# Revit family: H9726-V3
name_source: partatom
category: Plumbing Fixtures
revit_build: Autodesk Revit 2015 (Build: 20140606_1530(x64)
units: mm (PartAtom-declared; Revit-internal decimal feet)

## types (1)
- H9726-V3
    Category = Basin mixer
    DLB090016 = Brass, Chrome plated
    Default Elevation = 1219 mm
    Description = French manufacturer Delabie is a leader in the European sanitary ware market for non-domestic places. Water controls, solutions for disabled people, sanitary ware, for schools, leisure centres, offices, hospitals, airports…
    Diameter = 15 mm  [stored 0.0492126 ft]
    Features = Deck-mounted SECURITHERM dual control thermostatic basin mixer, with ergonomic pop-up waste 1 1/4" in brass.  Anti-scalding failsafe: hot water shuts off immediately if cold water supply fails. Swivelling spout L. 150mm H. 210mm with smooth interior and with BIOSAFE hygienic outlet, suitable for fitting a BIOFIL filter (reduces bacterial development).  Scale-resistant thermostatic cartridge for temperature control.  ¼-turn ceramic head for adjusting the flow rate.  Temperature can be adjusted, with two temperature limiters: first temperature limiter set at to 38°C (can be overidden), and second temperature limiter set at 41°C.  Thermal shocks are possible.  Flow rate regulated at 5 lpm.  ERGO controls.  Reinforced fixing via 2 stainless steel rods. PEX F3/8" with filters and non-return valves.
    Finish = Chrome-plated
    FlowRate = 5 lpm
    Grade = ACS, TMV3, WRAS, BELGAQUA, PZH, HKWSD
    IntegralAccessories = Waste, PEX flexibles
    Manufacturer = DELABIE
    ManufacturerName = DELABIE
    Material = Brass
    Model = SECURITHERM
    Model number = H9726
    Name = H9726
    NominalHeight = 21 cm
    NominalWidth = 15 cm
    Operation = Dual control thermostatic mixer
    Polantis code = DLB090016
    ProductInformation = http://www.delabie.com
    SerialNumber = 3456330115117
    URL = http://www.delabie.com
    WarrantyDescription = Any manufacturing defect
    WarrantyDurationUnit = 10 years
    WaterSupplyTemperatureMaximum = 55°C-85° (∆50°C : CW/HW)

note: [stored X ft] marks values corroborated as IEEE doubles in the binary element streams (Revit-internal decimal feet)

## geometry (parser evidence)
native form markers: Sweep x4
no freeform markers — native parametric forms only
